# Revit family: Sink-Under_Mount-Kitchen-KOHLER-Vault-K-3822
name_source: partatom
category: Plumbing Fixtures
revit_build: Autodesk Revit 2015 (Build: 20140606_1530(x64)
units: mm (PartAtom-declared; Revit-internal decimal feet)

## types (1)
- NA-Stainless Steel
    ADA Compliant = No
    Assembly Code = D2010400
    CW Connection = No
    Cold Water Inlet = Cold Water Inlet
    Date Modified = 04/15/2019
    Default Elevation = 36"
    Description = 24 inch x 18-1/4 inch x 9-3/8 inch under-mount medium single-bowl kitchen sink with no faucet holes
    Drain Included = No
    Finish = Kohler-Metal-NA-Stainless
    HW Connection = No
    Height = 9 3/8"
    Hot Water Inlet = Hot Water Inlet
    Length = 24"
    Manufacturer = KOHLER Co.
    MasterFormat 1995 = 15410
    MasterFormat 2004 = 22.41.16
    Material = 18-Gauge Stainless Steel
    Model = K-3822-NA
    Product Documentation Link = https://www.us.kohler.com
    Product Name = Vault
    Product Page URL = http://www.us.kohler.com
    URL = https://www.us.kohler.com
    Vent Connection = No
    Waste Connection = Yes
    Waste Water Outlet = Waste Water Outlet
    WaterSense Certified = No
    Width = 18 1/4"

## geometry (parser evidence)
native form markers: Sweep x5
no freeform markers — native parametric forms only
